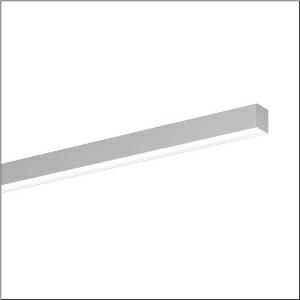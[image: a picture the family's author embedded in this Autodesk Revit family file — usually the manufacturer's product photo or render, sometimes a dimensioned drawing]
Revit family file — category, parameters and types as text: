
# Revit family: silica_21_51mx23tctas
name_source: partatom
category: Lighting Fixtures
units: mm (PartAtom-declared; Revit-internal decimal feet)

## family parameters
Cut with Voids When Loaded = No
Host = Face
Light Source = No
Part Type = Normal
Room Calculation Point = No
Round Connector Dimension = Use Diameter
Shared = No

## types (1)
- --- (1 x LED, 8070 lm, 81.1 W, 6500K)
    Apparent Load = 81 VA
    CIE Flux Codes = 78 96 99 100 100
    Color Rendering = 80
    Color Temperature = 6500K
    Default Elevation = 1800 mm
    Description = Silica 21, office luminaire, primary optical cover: prismatic diffuser, of PMMA, CAT 2 (L<= 3000cd/m²), light emission: direct distribution, primary light characteristic: symmetric, installation type: surface-mounted, LED, rated luminous flux: 8.070lm, luminous efficacy: 95lm/W, light colour: 8tw, colour temperature: 2700..6500K, control gear: DALI DT8, with terminal, 3+2-pole, max. 2.5mm², mains connection: 220..240V, AC, 50/60Hz, rated input power: 85.1W, luminaire housing, of aluminium, metallic grey (RAL 9006), length: 3.004mm, width: 53mm, height: 53mm, protection rating (complete): IP20, insulation class (complete): insulation class I (protective earthing), certification: CE, permissible operating ambient temperature: 0..+35°C, standard: EN 50419, packaging unit: 1 piece
    Height = 53 mm
    Lamp = 1 x LED
    Lamp Light Flux = 8070 lm
    Lamp Power = 81.1 W
    Lamp count = 1
    Length = 3004 mm
    Luminous efficacy = 100 lm/W
    Manufacturer = Siteco
    ModVariant = No
    Model = 51MX23TCTAS
    Mounting Place = Ceiling
    Mounting Type = Surface mounted
    Number of Poles = 1
    OnlyDefault = Yes
    Power Factor = 1
    Product Name = Silica 21
    Product group = office luminaire | ceiling mounted
    ProductGroupID = 301
    Protection Class = Protection class I
    Protection Degree = IP 20
    RLX_Detail_Level = 1
    RLX_Emergency_Light_Flux = 0 lm
    RLX_Emergency_Type = 0
    RLX_Emergency_Type_DB = No
    RlxData = <blob elided: 17873 chars, md5=ee78347d>
    Socket = socket
    Standby Power = 0 W
    System Light Flux = 8070 lm
    System Power = 81 W
    Type Comments = individual setting
    Type Image = l_1335933.jpg
    URL = http://relux.com
    VarID = @adj_139283
    Voltage = 0 V
    Weight = 0.00 kg
    Width = 53 mm

## geometry (parser evidence)
native form markers: Blend x4, Sweep x11
no freeform markers — native parametric forms only
